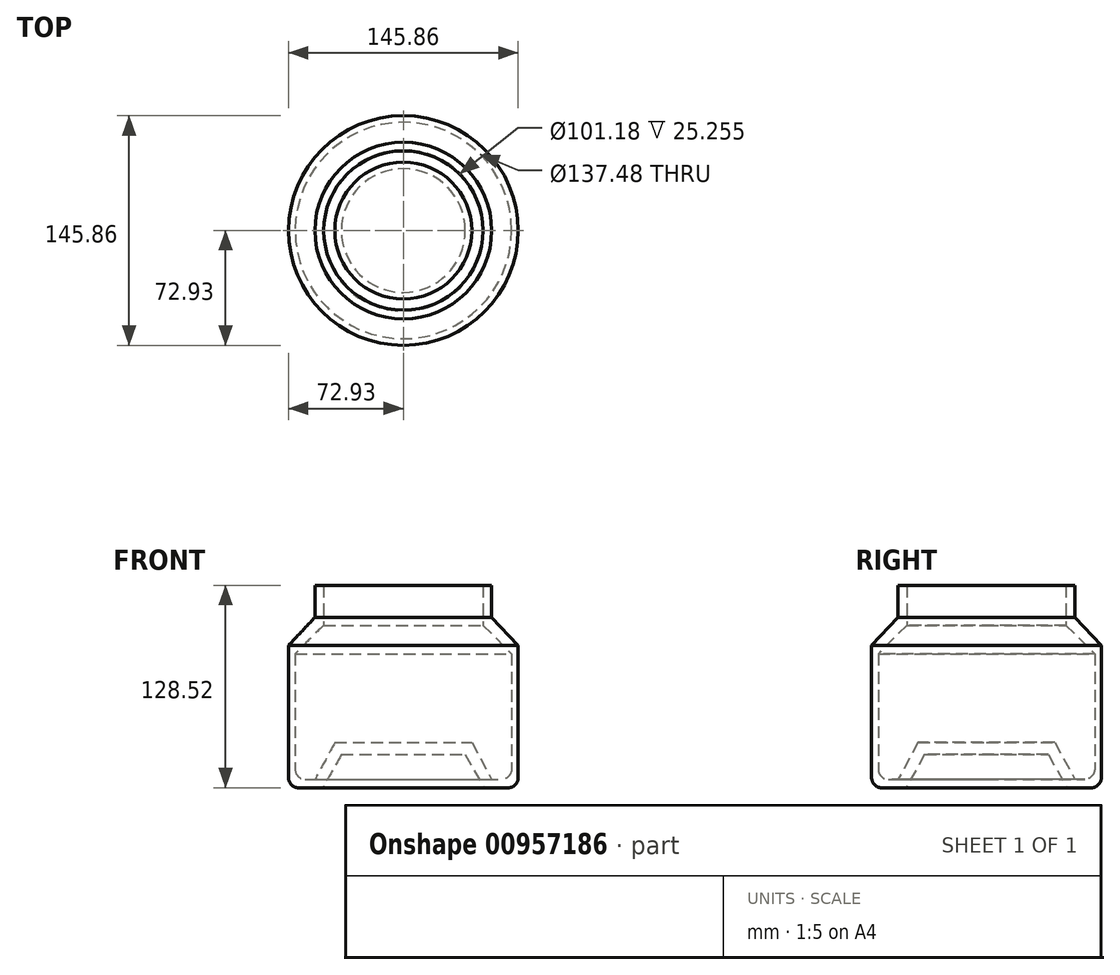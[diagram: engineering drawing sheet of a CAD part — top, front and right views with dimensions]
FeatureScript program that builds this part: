
annotation { "Feature Type Name" : "Feature", "Feature Type Description" : "" }
export const myFeature = defineFeature(function(context is Context, id is Id, definition is map)
    precondition{}
    {
        {
            var Q0;
            Q0=qCreatedBy(makeId("Front.planeOp"),FACE);
            var sketch = newSketch(context, id + "F0", { "sketchPlane" : qUnion([Q0])});
            skLineSegment(sketch, "E0", {"start": v(0, 0) * mm, "end": v(0, 71.8) * mm, "construction": true});
            skLineSegment(sketch, "E1", {"start": v(0, 0) * mm, "end": v(39.31, 0) * mm});
            skLineSegment(sketch, "E2", {"start": v(39.31, 0) * mm, "end": v(51.18, -21.12) * mm});
            skLineSegment(sketch, "E3", {"start": v(51.18, -21.12) * mm, "end": v(66.58, -21.12) * mm});
            skLineSegment(sketch, "E4", {"start": v(72.93, -14.77) * mm, "end": v(72.93, 69.34) * mm});
            skLineSegment(sketch, "E5", {"start": v(72.93, 69.34) * mm, "end": v(56.12, 87.13) * mm});
            skLineSegment(sketch, "E6", {"start": v(56.12, 87.13) * mm, "end": v(56.12, 107.4) * mm});
            skLineSegment(sketch, "E7", {"start": v(56.12, 107.4) * mm, "end": v(50.59, 107.4) * mm});
            skLineSegment(sketch, "E8", {"start": v(50.59, 107.4) * mm, "end": v(50.59, 82.15) * mm});
            skLineSegment(sketch, "E9", {"start": v(50.59, 82.15) * mm, "end": v(68.74, 64) * mm});
            skLineSegment(sketch, "E10", {"start": v(68.74, 64) * mm, "end": v(68.74, -9.37) * mm});
            skLineSegment(sketch, "E11", {"start": v(62.39, -15.72) * mm, "end": v(56.12, -15.72) * mm});
            skLineSegment(sketch, "E12", {"start": v(56.12, -15.72) * mm, "end": v(43.48, 7.57) * mm});
            skLineSegment(sketch, "E13", {"start": v(43.48, 7.57) * mm, "end": v(0, 7.57) * mm});
            skLineSegment(sketch, "E14", {"start": v(0, 7.57) * mm, "end": v(0, 0) * mm});
            skPoint(sketch, "E15.visualSharp", {"position": v(72.93, -21.12) * mm});
            skArc(sketch, "E15.filletArc", {"start": v(66.58, -21.12) * mm, "mid": v(71.07, -19.26) * mm, "end": v(72.93, -14.77) * mm});
            skPoint(sketch, "E16.visualSharp", {"position": v(68.74, -15.72) * mm});
            skArc(sketch, "E16.filletArc", {"start": v(62.39, -15.72) * mm, "mid": v(66.88, -13.86) * mm, "end": v(68.74, -9.37) * mm});
            skSolve(sketch);
        }
        {
            var Q0;
            Q0 = qSketchRegion(id + "F0", true);
            var Q1;
            Q1=sQuery(id+"F0.wireOp",EDGE,"E0");
            revolve(context, id + "F1", {"surfaceOperationType" : NewSurfaceOperationType.NEW, "entities" : qUnion([Q0]), "axis" : qUnion([Q1]), "revolveType" : RevolveType.FULL});
        }
    });
